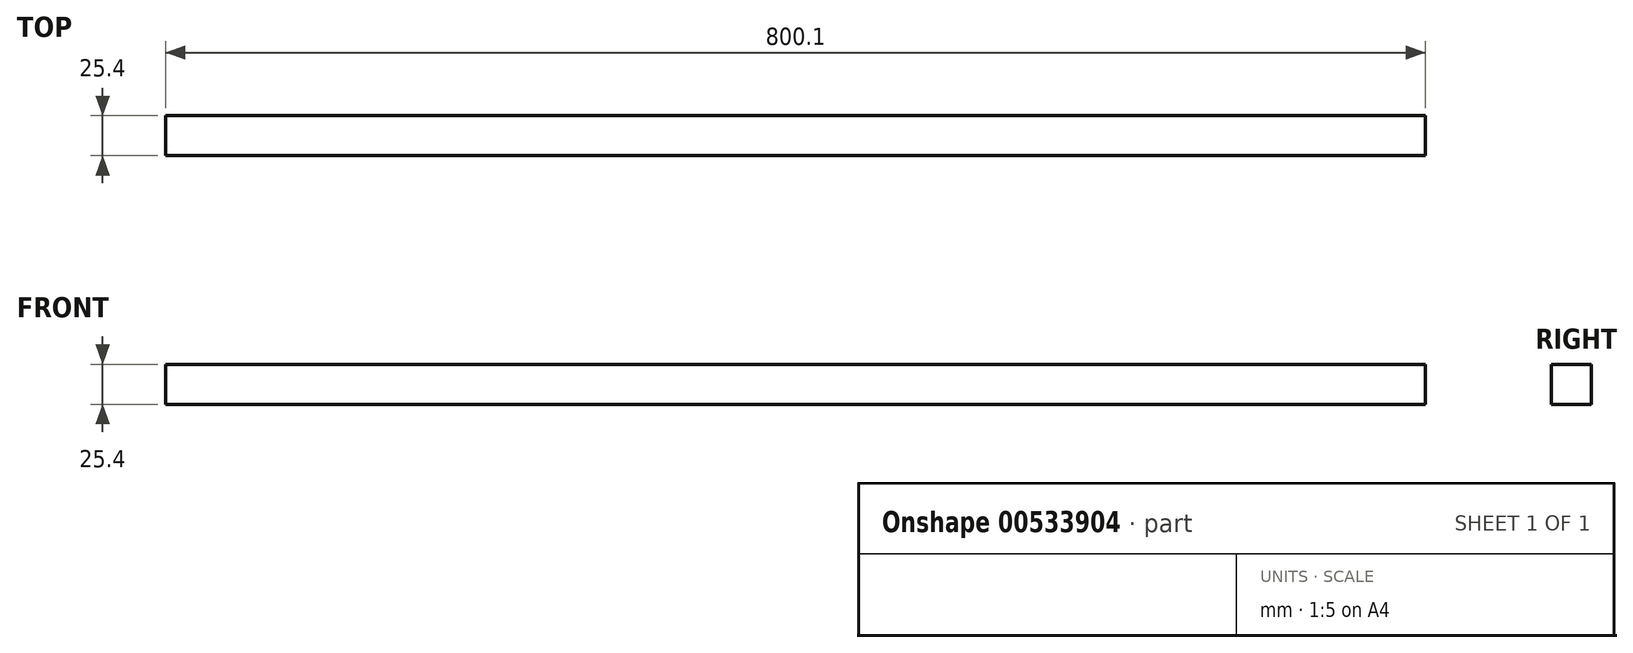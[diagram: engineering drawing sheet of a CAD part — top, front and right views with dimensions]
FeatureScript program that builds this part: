
annotation { "Feature Type Name" : "Feature", "Feature Type Description" : "" }
export const myFeature = defineFeature(function(context is Context, id is Id, definition is map)
    precondition{}
    {
        {
            var Q0;
            Q0=qCreatedBy(makeId("Top.planeOp"),FACE);
            var sketch = newSketch(context, id + "F0", { "sketchPlane" : qUnion([Q0])});
            skLineSegment(sketch, "E0.bottom", {"start": v(-400.05, -19.55) * mm, "end": v(400.05, -19.55) * mm});
            skLineSegment(sketch, "E0.top", {"start": v(-400.05, 5.85) * mm, "end": v(400.05, 5.85) * mm});
            skLineSegment(sketch, "E0.left", {"start": v(-400.05, -19.55) * mm, "end": v(-400.05, 5.85) * mm});
            skLineSegment(sketch, "E0.right", {"start": v(400.05, -19.55) * mm, "end": v(400.05, 5.85) * mm});
            skPoint(sketch, "E0.middle", {"position": v(0, -6.85) * mm});
            skSolve(sketch);
        }
        {
            var Q0;
            Q0=makeQuery(id+"F0.imprint","IMPRINT",FACE,{"disambiguationData":[TD([[makeQuery(id+"F0.imprint","IMPRINT",EDGE,{"derivedFrom":sQuery(id+"F0.wireOp",EDGE,"E0.bottom")}),1.0]])]});
            extrude(context, id + "F1", {"entities" : qUnion([Q0]), "depth" : 25.4 * mm, "offsetDistance" : 25.4 * mm});
        }
    });
